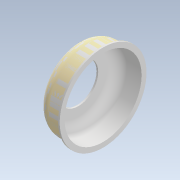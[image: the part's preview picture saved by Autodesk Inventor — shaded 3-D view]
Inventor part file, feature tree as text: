
AUTODESK INVENTOR PART (.ipt)
format: ipt  version: 2021 (Build 250183000, 183)  size: 172,544 bytes
history: native  units: mm
features: other x4, sketch x1
ambient origin geometry x8: Origin, YZ Plane, XZ Plane, XY Plane, X Axis, Y Axis, Z Axis, Center Point
bodies: Body1 (feature_tree), Body2 (feature_tree)
feature tree (5):
  other  "Sólido1"
  other  "Engrosado1"
  sketch  "Boceto1"  dims[d0=49.0mm d1=15.0mm d2=2.0mm d3=7.0mm d4=12.0mm d5=90.0deg d6=1.0mm d7=1.0mm]
  other  "Sup1"
  other  "SuperficieRevolución1"
